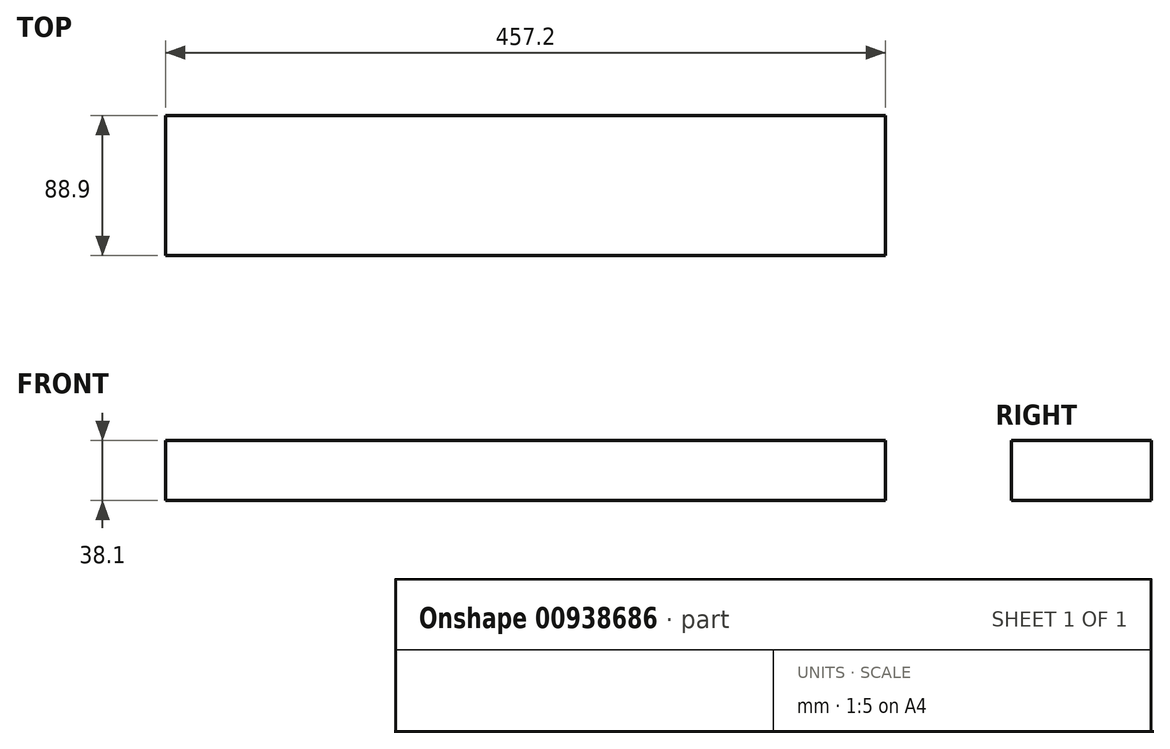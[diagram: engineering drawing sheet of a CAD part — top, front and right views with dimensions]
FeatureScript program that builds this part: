
annotation { "Feature Type Name" : "Feature", "Feature Type Description" : "" }
export const myFeature = defineFeature(function(context is Context, id is Id, definition is map)
    precondition{}
    {
        {
            var Q0;
            Q0=qCreatedBy(makeId("Right.planeOp"),FACE);
            var sketch = newSketch(context, id + "F0", { "sketchPlane" : qUnion([Q0])});
            skLineSegment(sketch, "E0.bottom", {"start": v(44.45, -19.05) * mm, "end": v(-44.45, -19.05) * mm});
            skLineSegment(sketch, "E0.top", {"start": v(44.45, 19.05) * mm, "end": v(-44.45, 19.05) * mm});
            skLineSegment(sketch, "E0.left", {"start": v(44.45, -19.05) * mm, "end": v(44.45, 19.05) * mm});
            skLineSegment(sketch, "E0.right", {"start": v(-44.45, -19.05) * mm, "end": v(-44.45, 19.05) * mm});
            skPoint(sketch, "E0.middle", {"position": v(0, 0) * mm});
            skSolve(sketch);
        }
        {
            var Q0;
            Q0=qSketchRegion(id+"F0",true);
            var Q1;
            Q1=makeQuery(id+"F0.imprint","IMPRINT",FACE,{"disambiguationData":[TD([[makeQuery(id+"F0.imprint","IMPRINT",EDGE,{"derivedFrom":sQuery(id+"F0.wireOp",EDGE,"E0.bottom")}),-1.0]])]});
            extrude(context, id + "F1", {"entities" : qUnion([Q0, Q1]), "depth" : 457.2 * mm, "offsetDistance" : 25.4 * mm});
        }
    });
